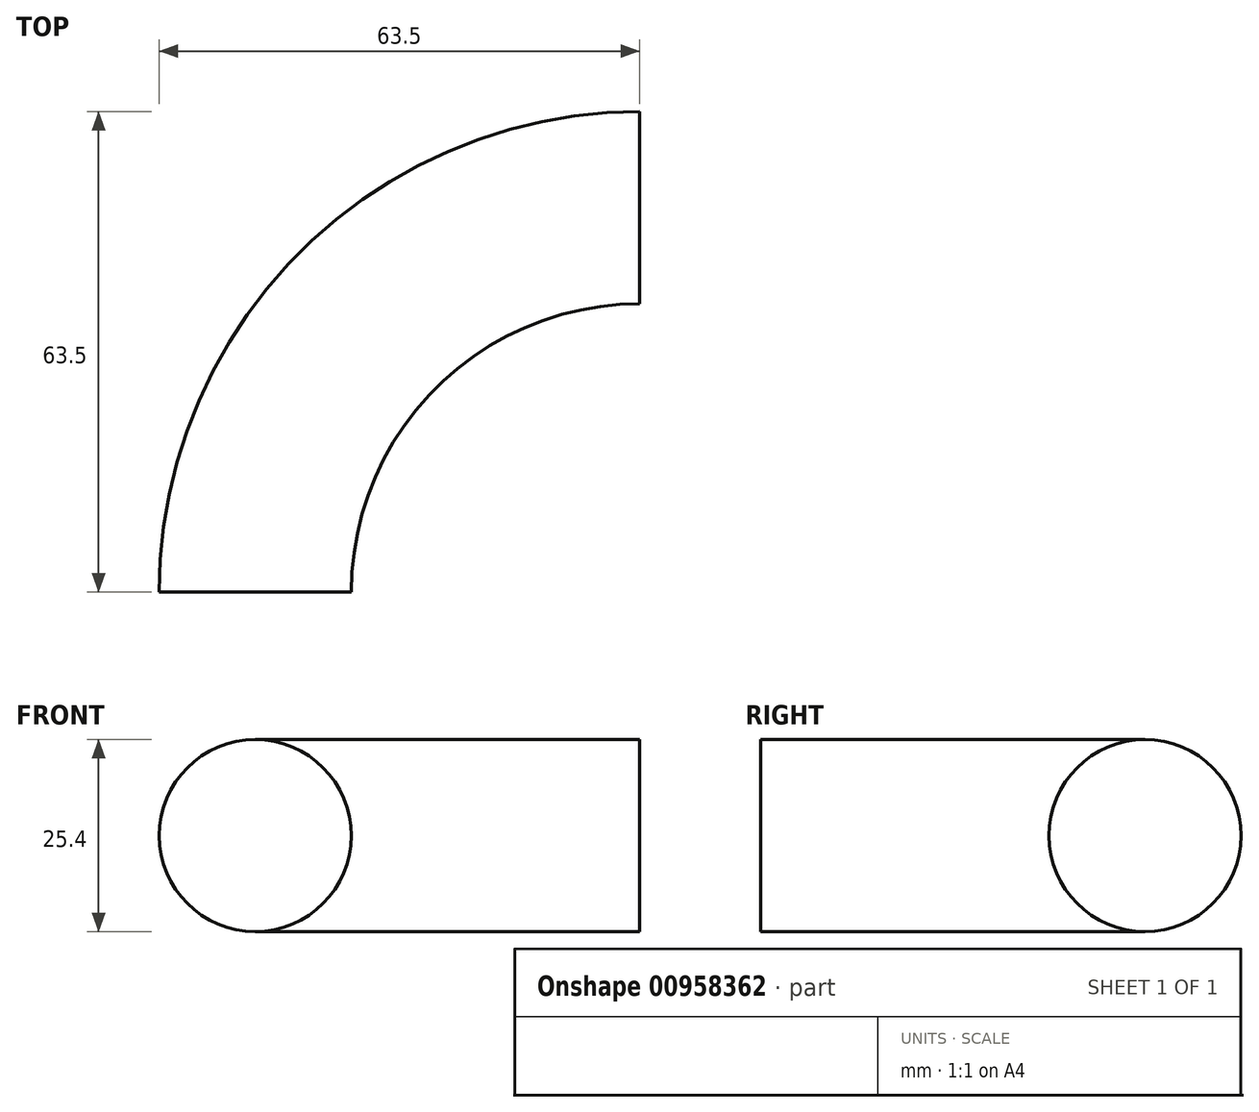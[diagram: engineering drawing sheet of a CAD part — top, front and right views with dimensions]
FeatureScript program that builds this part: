
annotation { "Feature Type Name" : "Feature", "Feature Type Description" : "" }
export const myFeature = defineFeature(function(context is Context, id is Id, definition is map)
    precondition{}
    {
        {
            var Q0;
            Q0=qCreatedBy(makeId("Front.planeOp"),FACE);
            var sketch = newSketch(context, id + "F0", { "sketchPlane" : qUnion([Q0])});
            skCircle(sketch, "E0", {"center": v(0, 0) * mm, "radius": 12.7 * mm});
            skSolve(sketch);
        }
        {
            var Q0;
            Q0=qCreatedBy(makeId("Right.planeOp"),FACE);
            cPlane(context, id + "F1", {"entities" : qUnion([Q0]), "cplaneType" : CPlaneType.OFFSET, "offset" : 50.8 * mm, "width" : 152.4 * mm, "height" : 152.4 * mm});
        }
        {
            var Q0;
            Q0=qCreatedBy(makeId("Top.planeOp"),FACE);
            var sketch = newSketch(context, id + "F2", { "sketchPlane" : qUnion([Q0])});
            skLineSegment(sketch, "E1", {"start": v(0, 0) * mm, "end": v(50.8, 0) * mm});
            skArc(sketch, "E2", {"start": v(50.8, 50.8) * mm, "mid": v(14.88, 35.92) * mm, "end": v(0, 0) * mm});
            skLineSegment(sketch, "E3", {"start": v(50.8, 0) * mm, "end": v(50.8, 50.8) * mm});
            skSolve(sketch);
        }
        {
            var Q0;
            Q0=makeQuery(id+"F0.imprint","IMPRINT",FACE,{"disambiguationData":[TD([[makeQuery(id+"F0.imprint","IMPRINT",EDGE,{"derivedFrom":sQuery(id+"F0.wireOp",EDGE,"E0")}),1.0]])]});
            var Q1;
            Q1=sQuery(id+"F2.wireOp",EDGE,"E2");
            sweep(context, id + "F3", {"profiles" : qUnion([Q0]), "path" : qUnion([Q1])});
        }
    });
